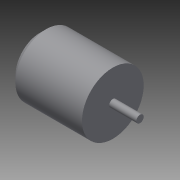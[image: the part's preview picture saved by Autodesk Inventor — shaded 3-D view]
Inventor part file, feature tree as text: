
AUTODESK INVENTOR PART (.ipt)
format: ipt  version: 2014 (Build 180170000, 170)  size: 87,552 bytes
history: native  units: in
note: dims shown in document units (in); Inventor stores cm internally (conversion verified against a paired STEP export)
features: revolve x1, chamfer x1, sketch x1
ambient origin geometry x8: Origin, YZ Plane, XZ Plane, XY Plane, X Axis, Y Axis, Z Axis, Center Point
bodies: Solid1 (feature_tree)
feature tree (3):
  revolve  "Revolution1"  [1 undecoded]
  chamfer  "Chamfer1"  Distance=0.1181in
  sketch  "Sketch1"  dims[d0=0.9843in d1=2.3228in d2=0.1181in d3=0.8661in d4=90.0deg d5=0.2in d6=0.125in d7=45.0deg]
note: 1 required parameter value undecoded (feature->parameter linkage not recoverable at this tier; creation-order binding heuristic only, values carry confidence <= 0.55)
